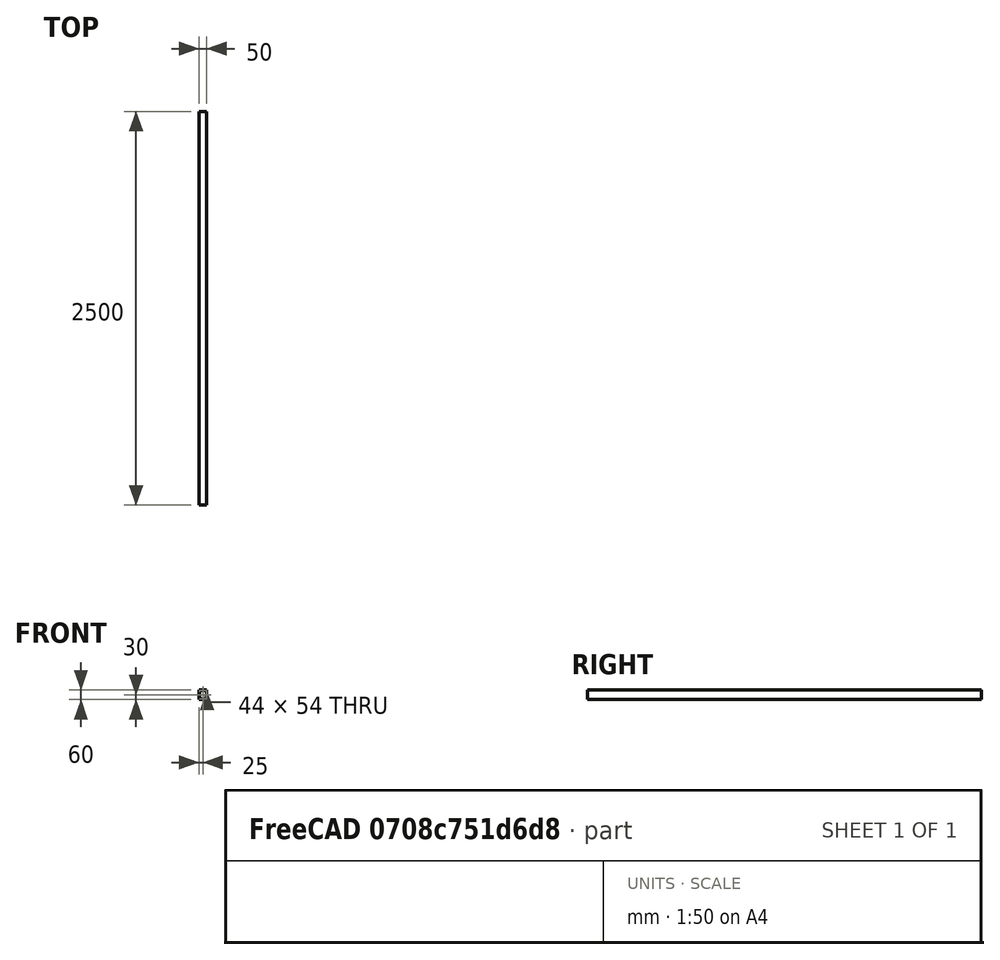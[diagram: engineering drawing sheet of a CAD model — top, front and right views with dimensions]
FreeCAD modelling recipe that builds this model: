
FCSTD DOCUMENT  (FreeCAD 0.20R29177 +426 (Git))
Label: beam
License: All rights reserved
LicenseURL: http://en.wikipedia.org/wiki/All_rights_reserved
objects: Sketcher::SketchObject×1, PartDesign::Pad×1, PartDesign::Body×1
note: 4 computed .brp shape members not serialized (recipe doc carries the construction recipe); baked Part::Feature solids carry a one-line shape summary decoded from their .brp

FEATURE [Sketcher::SketchObject] Sketch
  FullyConstrained = true
  MapMode = 5
  Placement = pos=(0,0,0) rot=(1,0,0;1.5708rad)
  Support = -> [XZ_Plane]
  sketch-geometry (8):
    g0: LineSegment StartX=0 StartY=0 StartZ=0 EndX=50 EndY=0 EndZ=0
    g1: LineSegment StartX=50 StartY=0 StartZ=0 EndX=50 EndY=60 EndZ=0
    g2: LineSegment StartX=50 StartY=60 StartZ=0 EndX=0 EndY=60 EndZ=0
    g3: LineSegment StartX=0 StartY=60 StartZ=0 EndX=0 EndY=0 EndZ=0
    g4: LineSegment StartX=3 StartY=57 StartZ=0 EndX=47 EndY=57 EndZ=0
    g5: LineSegment StartX=47 StartY=57 StartZ=0 EndX=47 EndY=3 EndZ=0
    g6: LineSegment StartX=47 StartY=3 StartZ=0 EndX=3 EndY=3 EndZ=0
    g7: LineSegment StartX=3 StartY=3 StartZ=0 EndX=3 EndY=57 EndZ=0
  constraints (23):
    c: Coincident(g0,g1)
    c: Coincident(g1,g2)
    c: Coincident(g2,g3)
    c: Coincident(g3,g0)
    c: Horizontal(g0)
    c: Horizontal(g2)
    c: Vertical(g1)
    c: Vertical(g3)
    c: Coincident(g0,g-1)
    c: DistanceX(g2,g2) = 50
    c: DistanceY(g1,g1) = 60
    c: Coincident(g4,g5)
    c: Coincident(g5,g6)
    c: Coincident(g6,g7)
    c: Coincident(g7,g4)
    c: Horizontal(g4)
    c: Horizontal(g6)
    c: Vertical(g5)
    c: Vertical(g7)
    c: DistanceY(g4,g1) = 3
    c: DistanceX(g4,g1) = 3
    c: DistanceX(g0,g6) = 3
    c: DistanceY(g0,g6) = 3
FEATURE [PartDesign::Pad] Pad
  Direction = (0,-1,-2e-16)
  Length = 2500
  Length2 = 10
  Placement = pos=(0,0,0) rot=(1,0,0;1.5708rad)
  Profile = -> Sketch
  ReferenceAxis = -> Sketch [N_Axis]
  Refine = true
  Type = 0
FEATURE [PartDesign::Body] Body
  Group = -> [Sketch,Pad]
  Origin = -> Origin
  Tip = -> Pad
